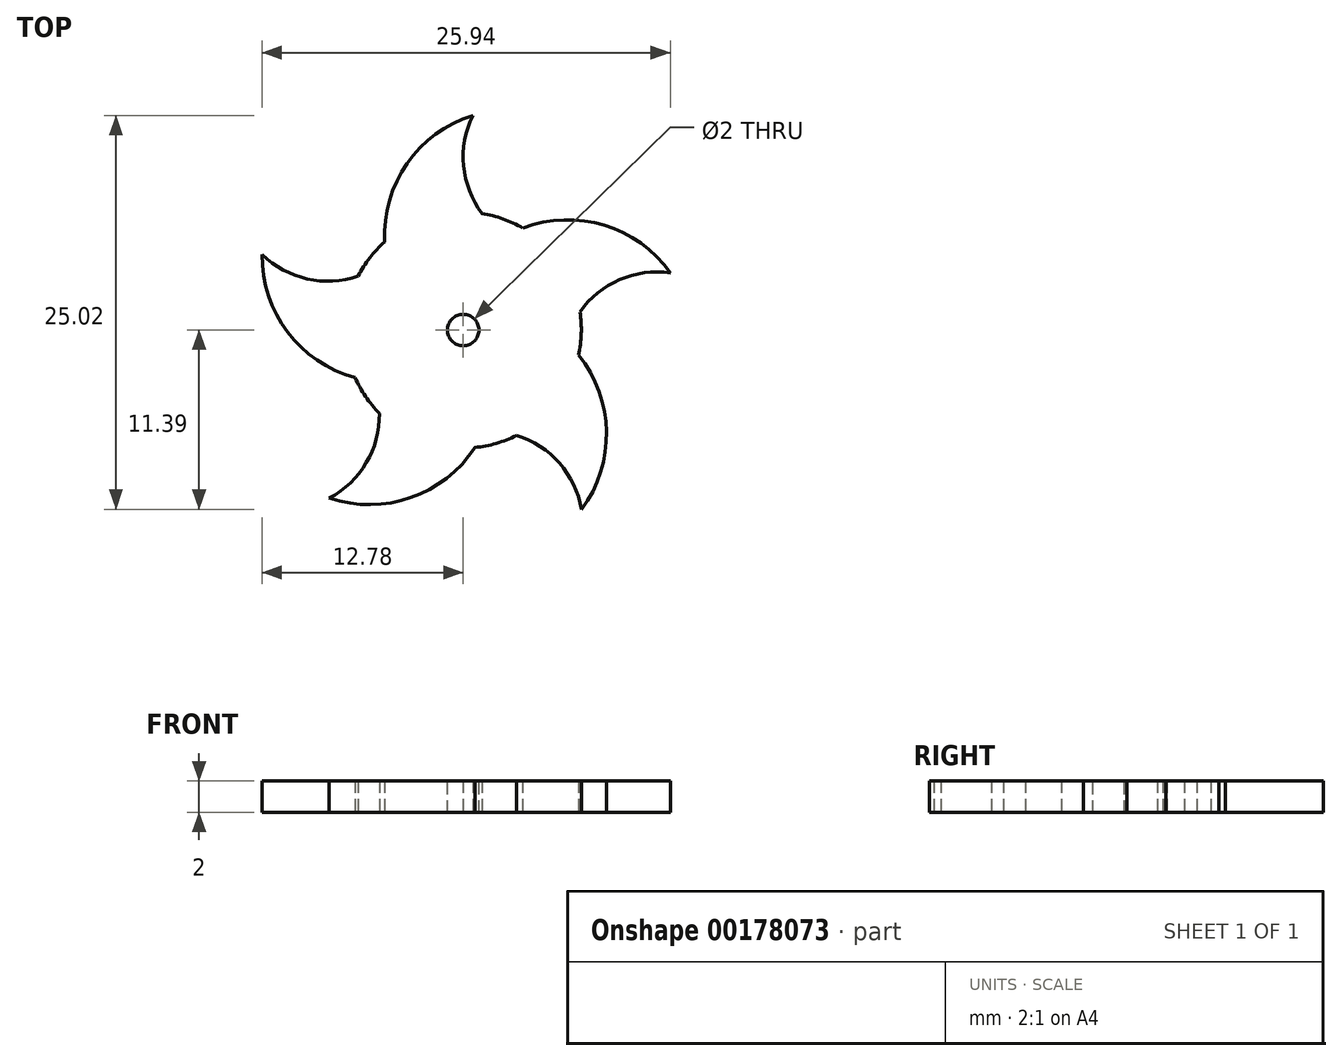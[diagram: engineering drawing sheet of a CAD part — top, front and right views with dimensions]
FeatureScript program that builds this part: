
annotation { "Feature Type Name" : "Feature", "Feature Type Description" : "" }
export const myFeature = defineFeature(function(context is Context, id is Id, definition is map)
    precondition{}
    {
        {
            var Q0;
            Q0=qCreatedBy(makeId("Top.planeOp"),FACE);
            var sketch = newSketch(context, id + "F0", { "sketchPlane" : qUnion([Q0])});
            skCircle(sketch, "E0", {"center": v(0, 0) * mm, "radius": 7.5 * mm});
            skLineSegment(sketch, "E1", {"start": v(0, 0) * mm, "end": v(0, 7.5) * mm, "construction": true});
            skArc(sketch, "E2", {"start": v(0.6, 13.63) * mm, "mid": v(-3.56, 10.57) * mm, "end": v(-4.99, 5.6) * mm});
            skArc(sketch, "E3", {"start": v(0.6, 13.63) * mm, "mid": v(0.03, 10.44) * mm, "end": v(1.2, 7.4) * mm});
            skArc(sketch, "E4.1.0", {"start": v(-12.78, 4.8) * mm, "mid": v(-11.16, -0.12) * mm, "end": v(-6.87, -3.02) * mm});
            skArc(sketch, "E4.1.1", {"start": v(-12.78, 4.8) * mm, "mid": v(-9.92, 3.25) * mm, "end": v(-6.67, 3.43) * mm});
            skArc(sketch, "E4.2.0", {"start": v(-8.5, -10.67) * mm, "mid": v(-3.33, -10.65) * mm, "end": v(0.75, -7.46) * mm});
            skArc(sketch, "E4.2.1", {"start": v(-8.5, -10.67) * mm, "mid": v(-6.16, -8.43) * mm, "end": v(-5.32, -5.29) * mm});
            skArc(sketch, "E4.3.0", {"start": v(7.52, -11.39) * mm, "mid": v(9.1, -6.46) * mm, "end": v(7.33, -1.6) * mm});
            skArc(sketch, "E4.3.1", {"start": v(7.52, -11.39) * mm, "mid": v(6.11, -8.46) * mm, "end": v(3.38, -6.7) * mm});
            skArc(sketch, "E4.4.0", {"start": v(13.16, 3.63) * mm, "mid": v(8.95, 6.66) * mm, "end": v(3.78, 6.48) * mm});
            skArc(sketch, "E4.4.1", {"start": v(13.16, 3.63) * mm, "mid": v(9.93, 3.2) * mm, "end": v(7.41, 1.15) * mm});
            skSolve(sketch);
        }
        {
            var Q0;
            Q0 = qSketchRegion(id + "F0", true);
            extrude(context, id + "F1", {"entities" : qUnion([Q0]), "depth" : 2 * mm});
        }
        {
            var Q0;
            Q0=makeQuery(id+"F1.opExtrude","CAP_FACE",FACE,{"disambiguationData":[OSD([sQuery(id+"F0.wireOp",EDGE,"E0"),sQuery(id+"F0.wireOp",EDGE,"E2"),sQuery(id+"F0.wireOp",EDGE,"E3"),sQuery(id+"F0.wireOp",EDGE,"E4.1.0"),sQuery(id+"F0.wireOp",EDGE,"E4.1.1"),sQuery(id+"F0.wireOp",EDGE,"E4.2.0"),sQuery(id+"F0.wireOp",EDGE,"E4.2.1"),sQuery(id+"F0.wireOp",EDGE,"E4.3.0"),sQuery(id+"F0.wireOp",EDGE,"E4.3.1"),sQuery(id+"F0.wireOp",EDGE,"E4.4.0"),sQuery(id+"F0.wireOp",EDGE,"E4.4.1")])],"isStart":false});
            var sketch = newSketch(context, id + "F2", { "sketchPlane" : qUnion([Q0])});
            skCircle(sketch, "E5", {"center": v(0, 0) * mm, "radius": 1 * mm});
            skSolve(sketch);
        }
        {
            var Q0;
            Q0 = qSketchRegion(id + "F2", true);
            extrude(context, id + "F3", {"entities" : qUnion([Q0]), "operationType" : NewBodyOperationType.REMOVE, "endBound" : BoundingType.THROUGH_ALL, "oppositeDirection" : true, "depth" : 25 * mm});
        }
    });
